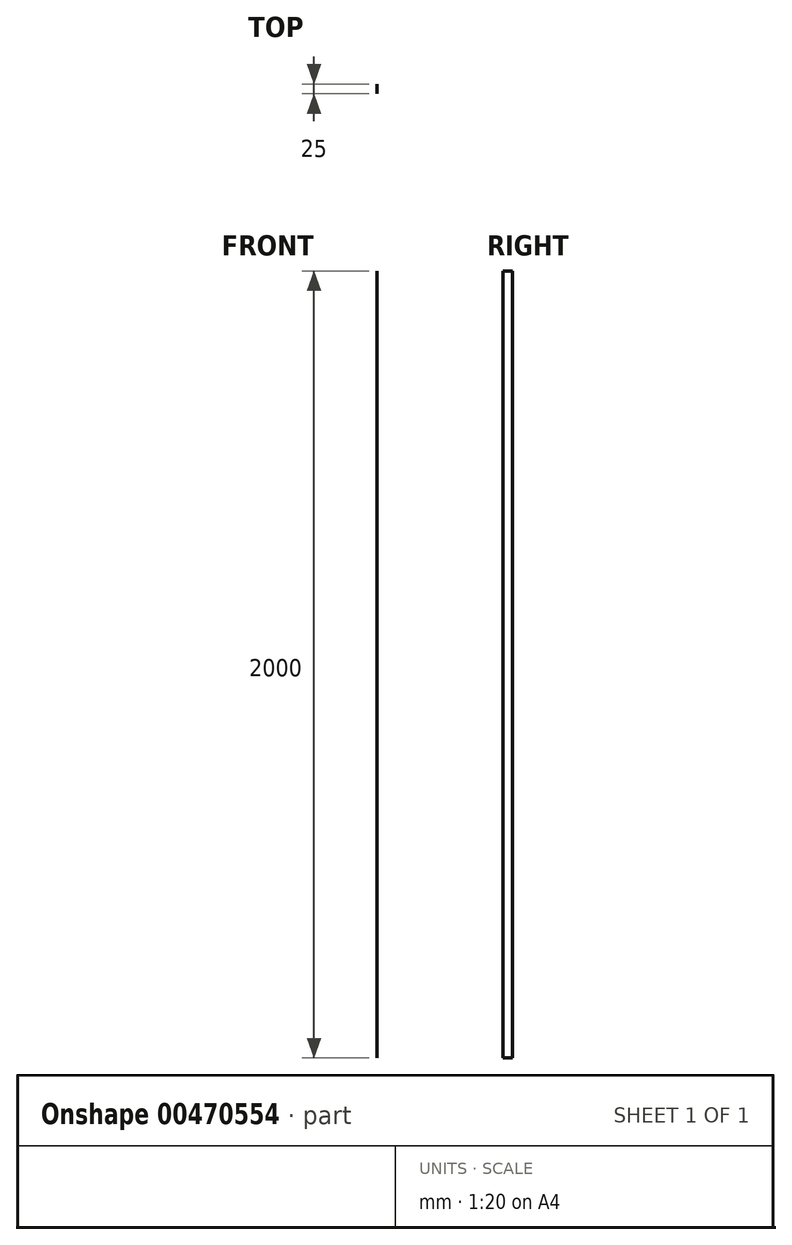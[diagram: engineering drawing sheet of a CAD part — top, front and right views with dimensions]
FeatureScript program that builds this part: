
annotation { "Feature Type Name" : "Feature", "Feature Type Description" : "" }
export const myFeature = defineFeature(function(context is Context, id is Id, definition is map)
    precondition{}
    {
        {
            var Q0;
            Q0=qCreatedBy(makeId("Front.planeOp"),FACE);
            var sketch = newSketch(context, id + "F0", { "sketchPlane" : qUnion([Q0])});
            skLineSegment(sketch, "E0", {"start": v(-68.68, 49.78) * mm, "end": v(2031.32, 49.78) * mm});
            skLineSegment(sketch, "E1", {"start": v(2031.32, 49.78) * mm, "end": v(2031.32, 24.78) * mm});
            skLineSegment(sketch, "E2", {"start": v(2031.32, 24.78) * mm, "end": v(-68.68, 24.78) * mm});
            skLineSegment(sketch, "E3", {"start": v(-68.68, 24.78) * mm, "end": v(-68.68, 49.78) * mm});
            skLineSegment(sketch, "E4", {"start": v(25.63, 49.78) * mm, "end": v(25.63, 2049.78) * mm});
            skLineSegment(sketch, "E5.0", {"start": v(9.63, 49.78) * mm, "end": v(9.63, 2049.78) * mm});
            skLineSegment(sketch, "E6.0", {"start": v(20.63, 49.78) * mm, "end": v(20.63, 2049.78) * mm});
            skSolve(sketch);
        }
        {
            var Q0;
            Q0=sQuery(id+"F0.wireOp",EDGE,"E6.0");
            extrude(context, id + "F1", {"bodyType" : ToolBodyType.SURFACE, "surfaceEntities" : qUnion([Q0]), "depth" : 25 * mm});
        }
    });
